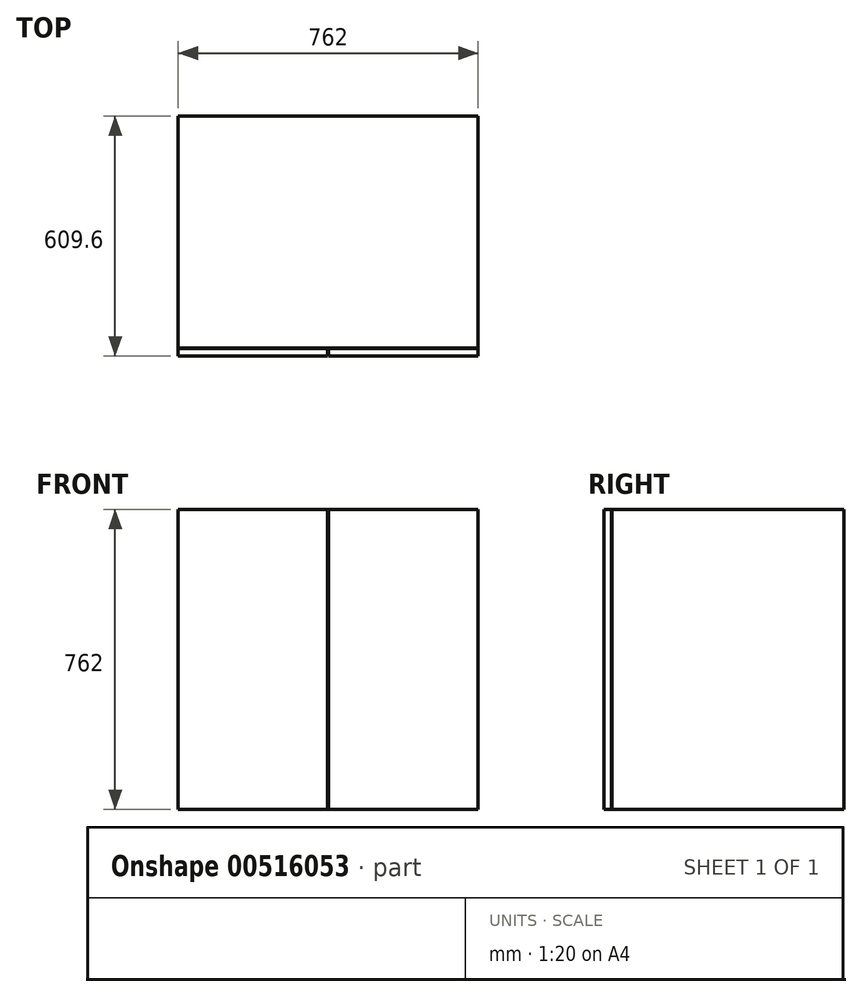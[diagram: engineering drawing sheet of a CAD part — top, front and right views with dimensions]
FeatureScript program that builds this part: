
annotation { "Feature Type Name" : "Feature", "Feature Type Description" : "" }
export const myFeature = defineFeature(function(context is Context, id is Id, definition is map)
    precondition{}
    {
        {
            var Q0;
            Q0=qCreatedBy(makeId("Top.planeOp"),FACE);
            var sketch = newSketch(context, id + "F0", { "sketchPlane" : qUnion([Q0])});
            skLineSegment(sketch, "E0.bottom", {"start": v(382.27, -296.54) * mm, "end": v(2.54, -296.55) * mm});
            skLineSegment(sketch, "E0.top", {"start": v(382.27, 294) * mm, "end": v(-379.73, 294) * mm});
            skLineSegment(sketch, "E0.left", {"start": v(382.27, -295.27) * mm, "end": v(382.27, 294) * mm});
            skLineSegment(sketch, "E0.right", {"start": v(-379.73, -295.28) * mm, "end": v(-379.73, 294) * mm});
            skPoint(sketch, "E0.middle", {"position": v(1.27, -0.63) * mm});
            skLineSegment(sketch, "E1.bottom", {"start": v(-379.73, -296.55) * mm, "end": v(0, -296.55) * mm});
            skLineSegment(sketch, "E1.top", {"start": v(-379.73, -315.6) * mm, "end": v(0, -315.6) * mm});
            skLineSegment(sketch, "E1.left", {"start": v(-379.73, -296.55) * mm, "end": v(-379.73, -315.6) * mm});
            skLineSegment(sketch, "E1.right", {"start": v(2.54, -296.55) * mm, "end": v(2.54, -315.6) * mm});
            skLineSegment(sketch, "E2.MirrorCS", {"start": v(382.27, -296.54) * mm, "end": v(382.27, -315.6) * mm});
            skLineSegment(sketch, "E3.MirrorCS", {"start": v(382.27, -315.6) * mm, "end": v(2.54, -315.6) * mm});
            skLineSegment(sketch, "E4.MirrorCS", {"start": v(382.27, -296.54) * mm, "end": v(2.54, -296.54) * mm});
            skLineSegment(sketch, "E5", {"start": v(0, -315.6) * mm, "end": v(0, -296.55) * mm});
            skLineSegment(sketch, "E6", {"start": v(-379.73, -295.28) * mm, "end": v(382.27, -295.27) * mm});
            skLineSegment(sketch, "E7.trimOffspring", {"start": v(0, -296.55) * mm, "end": v(-379.73, -296.55) * mm});
            skSolve(sketch);
        }
        {
            var Q0;
            Q0=makeQuery(id+"F0.imprint","IMPRINT",FACE,{"disambiguationData":[TD([[makeQuery(id+"F0.imprint","IMPRINT",EDGE,{"derivedFrom":sQuery(id+"F0.wireOp",EDGE,"E0.top")}),1.0]])]});
            var Q1;
            Q1=makeQuery(id+"F0.imprint","IMPRINT",FACE,{"disambiguationData":[TD([[makeQuery(id+"F0.imprint","IMPRINT",EDGE,{"derivedFrom":sQuery(id+"F0.wireOp",EDGE,"E1.right")}),1.0]])]});
            var Q2;
            Q2=makeQuery(id+"F0.imprint","IMPRINT",FACE,{"disambiguationData":[TD([[makeQuery(id+"F0.imprint","IMPRINT",EDGE,{"derivedFrom":sQuery(id+"F0.wireOp",EDGE,"E1.top")}),1.0]])]});
            extrude(context, id + "F1", {"entities" : qUnion([Q0, Q1, Q2]), "depth" : 762 * mm, "offsetDistance" : 25.4 * mm});
        }
    });
